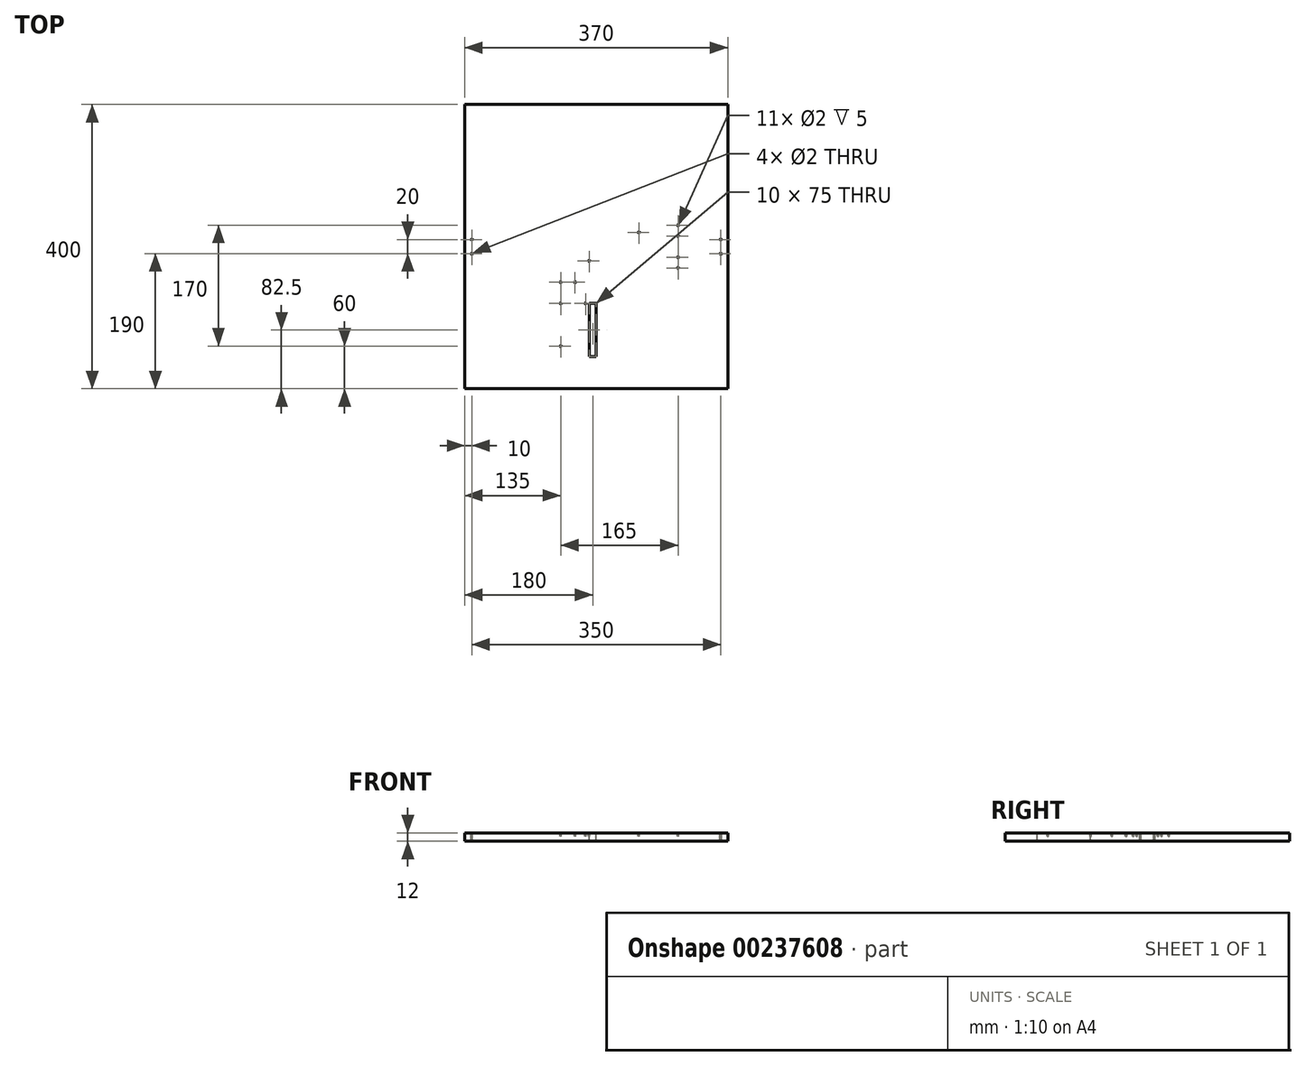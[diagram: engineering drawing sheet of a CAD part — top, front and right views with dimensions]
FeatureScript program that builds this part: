
annotation { "Feature Type Name" : "Feature", "Feature Type Description" : "" }
export const myFeature = defineFeature(function(context is Context, id is Id, definition is map)
    precondition{}
    {
        {
            var Q0;
            Q0=qCreatedBy(makeId("Top.planeOp"),FACE);
            var sketch = newSketch(context, id + "F0", { "sketchPlane" : qUnion([Q0])});
            skLineSegment(sketch, "E0", {"start": v(185, 200) * mm, "end": v(-185, 200) * mm});
            skLineSegment(sketch, "E1", {"start": v(-185, 200) * mm, "end": v(-185, -200) * mm});
            skLineSegment(sketch, "E2", {"start": v(-185, -200) * mm, "end": v(185, -200) * mm});
            skLineSegment(sketch, "E3", {"start": v(185, 200) * mm, "end": v(185, -200) * mm});
            skSolve(sketch);
        }
        {
            var Q0;
            Q0 = qSketchRegion(id + "F0", true);
            extrude(context, id + "F1", {"entities" : qUnion([Q0]), "depth" : 12 * mm});
        }
        {
            var Q0;
            Q0=makeQuery(id+"F1.opExtrude","CAP_FACE",FACE,{"disambiguationData":[OSD([sQuery(id+"F0.wireOp",EDGE,"E0"),sQuery(id+"F0.wireOp",EDGE,"E1"),sQuery(id+"F0.wireOp",EDGE,"E2"),sQuery(id+"F0.wireOp",EDGE,"E3")])],"isStart":false});
            var sketch = newSketch(context, id + "F2", { "sketchPlane" : qUnion([Q0])});
            skLineSegment(sketch, "E4", {"start": v(-10, -155) * mm, "end": v(0, -155) * mm});
            skLineSegment(sketch, "E5", {"start": v(0, -155) * mm, "end": v(0, -80) * mm});
            skLineSegment(sketch, "E6", {"start": v(0, -80) * mm, "end": v(-10, -80) * mm});
            skLineSegment(sketch, "E7", {"start": v(-10, -80) * mm, "end": v(-10, -155) * mm});
            skSolve(sketch);
        }
        {
            var Q0;
            Q0 = qSketchRegion(id + "F2", true);
            extrude(context, id + "F3", {"entities" : qUnion([Q0]), "operationType" : NewBodyOperationType.REMOVE, "oppositeDirection" : true, "depth" : 25 * mm});
        }
        {
            var Q0;
            Q0=makeQuery(id+"F1.opExtrude","CAP_FACE",FACE,{"disambiguationData":[OSD([sQuery(id+"F0.wireOp",EDGE,"E0"),sQuery(id+"F0.wireOp",EDGE,"E1"),sQuery(id+"F0.wireOp",EDGE,"E2"),sQuery(id+"F0.wireOp",EDGE,"E3")])],"isStart":false});
            var sketch = newSketch(context, id + "F4", { "sketchPlane" : qUnion([Q0])});
            skCircle(sketch, "E8", {"center": v(-50, -80) * mm, "radius": 1 * mm});
            skCircle(sketch, "E9", {"center": v(-15, -80) * mm, "radius": 1 * mm});
            skCircle(sketch, "E10", {"center": v(-50, -140) * mm, "radius": 1 * mm});
            skCircle(sketch, "E11", {"center": v(-30, -50) * mm, "radius": 1 * mm});
            skCircle(sketch, "E12", {"center": v(-50, -50) * mm, "radius": 1 * mm});
            skSolve(sketch);
        }
        {
            var Q0;
            Q0 = qSketchRegion(id + "F4", true);
            extrude(context, id + "F5", {"entities" : qUnion([Q0]), "operationType" : NewBodyOperationType.REMOVE, "oppositeDirection" : true, "depth" : 5 * mm});
        }
        {
            var Q0;
            Q0=makeQuery(id+"F1.opExtrude","CAP_FACE",FACE,{"disambiguationData":[OSD([sQuery(id+"F0.wireOp",EDGE,"E0"),sQuery(id+"F0.wireOp",EDGE,"E1"),sQuery(id+"F0.wireOp",EDGE,"E2"),sQuery(id+"F0.wireOp",EDGE,"E3")])],"isStart":false});
            var sketch = newSketch(context, id + "F6", { "sketchPlane" : qUnion([Q0])});
            skCircle(sketch, "E13", {"center": v(-175, -10) * mm, "radius": 1 * mm});
            skCircle(sketch, "E14", {"center": v(-175, 10) * mm, "radius": 1 * mm});
            skSolve(sketch);
        }
        {
            var Q0;
            Q0 = qSketchRegion(id + "F6", true);
            extrude(context, id + "F7", {"entities" : qUnion([Q0]), "operationType" : NewBodyOperationType.REMOVE, "oppositeDirection" : true, "depth" : 25 * mm});
        }
        {
            var Q0;
            Q0=makeQuery(id+"F1.opExtrude","CAP_FACE",FACE,{"disambiguationData":[OSD([sQuery(id+"F0.wireOp",EDGE,"E0"),sQuery(id+"F0.wireOp",EDGE,"E1"),sQuery(id+"F0.wireOp",EDGE,"E2"),sQuery(id+"F0.wireOp",EDGE,"E3")])],"isStart":false});
            var sketch = newSketch(context, id + "F8", { "sketchPlane" : qUnion([Q0])});
            skCircle(sketch, "E15", {"center": v(175, 10) * mm, "radius": 1 * mm});
            skCircle(sketch, "E16", {"center": v(175, -10) * mm, "radius": 1 * mm});
            skSolve(sketch);
        }
        {
            var Q0;
            Q0 = qSketchRegion(id + "F8", true);
            extrude(context, id + "F9", {"entities" : qUnion([Q0]), "operationType" : NewBodyOperationType.REMOVE, "oppositeDirection" : true, "depth" : 25 * mm});
        }
        {
            var Q0;
            Q0=makeQuery(id+"F1.opExtrude","CAP_FACE",FACE,{"disambiguationData":[OSD([sQuery(id+"F0.wireOp",EDGE,"E0"),sQuery(id+"F0.wireOp",EDGE,"E1"),sQuery(id+"F0.wireOp",EDGE,"E2"),sQuery(id+"F0.wireOp",EDGE,"E3")])],"isStart":false});
            var sketch = newSketch(context, id + "F10", { "sketchPlane" : qUnion([Q0])});
            skCircle(sketch, "E17", {"center": v(60, 20) * mm, "radius": 1 * mm});
            skCircle(sketch, "E18", {"center": v(-10, -20) * mm, "radius": 1 * mm});
            skSolve(sketch);
        }
        {
            var Q0;
            Q0 = qSketchRegion(id + "F10", true);
            extrude(context, id + "F11", {"entities" : qUnion([Q0]), "operationType" : NewBodyOperationType.REMOVE, "oppositeDirection" : true, "depth" : 5 * mm});
        }
        {
            var Q0;
            Q0=makeQuery(id+"F1.opExtrude","CAP_FACE",FACE,{"disambiguationData":[OSD([sQuery(id+"F0.wireOp",EDGE,"E0"),sQuery(id+"F0.wireOp",EDGE,"E1"),sQuery(id+"F0.wireOp",EDGE,"E2"),sQuery(id+"F0.wireOp",EDGE,"E3")])],"isStart":false});
            var sketch = newSketch(context, id + "F12", { "sketchPlane" : qUnion([Q0])});
            skCircle(sketch, "E19", {"center": v(115, -15) * mm, "radius": 1 * mm});
            skCircle(sketch, "E20", {"center": v(115, -30) * mm, "radius": 1 * mm});
            skSolve(sketch);
        }
        {
            var Q0;
            Q0 = qSketchRegion(id + "F12", true);
            extrude(context, id + "F13", {"entities" : qUnion([Q0]), "operationType" : NewBodyOperationType.REMOVE, "oppositeDirection" : true, "depth" : 5 * mm});
        }
        {
            var Q0;
            Q0=makeQuery(id+"F1.opExtrude","CAP_FACE",FACE,{"disambiguationData":[OSD([sQuery(id+"F0.wireOp",EDGE,"E0"),sQuery(id+"F0.wireOp",EDGE,"E1"),sQuery(id+"F0.wireOp",EDGE,"E2"),sQuery(id+"F0.wireOp",EDGE,"E3")])],"isStart":false});
            var sketch = newSketch(context, id + "F14", { "sketchPlane" : qUnion([Q0])});
            skCircle(sketch, "E21", {"center": v(115, 30) * mm, "radius": 1 * mm});
            skCircle(sketch, "E22", {"center": v(115, 15) * mm, "radius": 1 * mm});
            skSolve(sketch);
        }
        {
            var Q0;
            Q0 = qSketchRegion(id + "F14", true);
            extrude(context, id + "F15", {"entities" : qUnion([Q0]), "operationType" : NewBodyOperationType.REMOVE, "oppositeDirection" : true, "depth" : 5 * mm});
        }
    });
